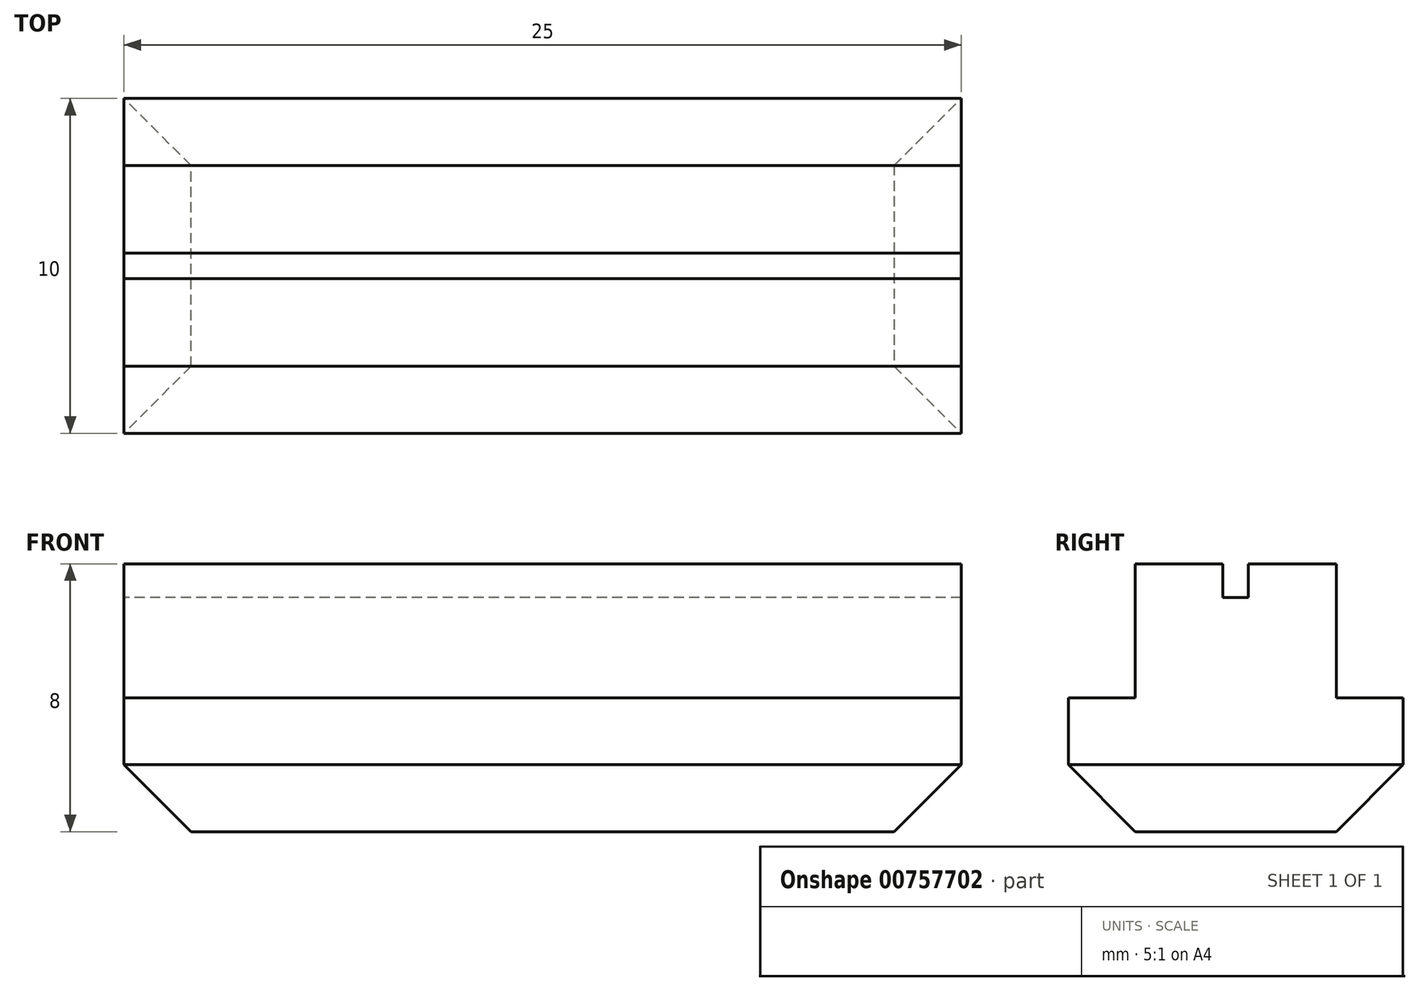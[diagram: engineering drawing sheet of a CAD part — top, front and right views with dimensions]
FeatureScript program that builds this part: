
annotation { "Feature Type Name" : "Feature", "Feature Type Description" : "" }
export const myFeature = defineFeature(function(context is Context, id is Id, definition is map)
    precondition{}
    {
        {
            var Q0;
            Q0=qCreatedBy(makeId("Front.planeOp"),FACE);
            var sketch = newSketch(context, id + "F0", { "sketchPlane" : qUnion([Q0])});
            skLineSegment(sketch, "E0.bottom", {"start": v(-12.5, 26) * mm, "end": v(12.5, 26) * mm});
            skLineSegment(sketch, "E0.top", {"start": v(-12.5, 34) * mm, "end": v(12.5, 34) * mm});
            skLineSegment(sketch, "E0.left", {"start": v(-12.5, 26) * mm, "end": v(-12.5, 34) * mm});
            skLineSegment(sketch, "E0.right", {"start": v(12.5, 26) * mm, "end": v(12.5, 34) * mm});
            skPoint(sketch, "E0.middle", {"position": v(0, 30) * mm});
            skSolve(sketch);
        }
        {
            var Q0;
            Q0=makeQuery(id+"F0.imprint","IMPRINT",FACE,{"disambiguationData":[TD([[makeQuery(id+"F0.imprint","IMPRINT",EDGE,{"derivedFrom":sQuery(id+"F0.wireOp",EDGE,"E0.bottom")}),1.0]])]});
            extrude(context, id + "F1", {"entities" : qUnion([Q0]), "endBound" : BoundingType.SYMMETRIC, "depth" : 10 * mm, "offsetDistance" : 25 * mm});
        }
        {
            var Q0;
            Q0=makeQuery(id+"F1.opExtrude","SWEPT_EDGE",EDGE,{"disambiguationData":[OSD([sQuery(id+"F0.wireOp",EDGE,"E0.bottom"),sQuery(id+"F0.wireOp",EDGE,"E0.right")])]});
            var Q1;
            Q1=makeQuery(id+"F1.opExtrude","SWEPT_EDGE",EDGE,{"disambiguationData":[OSD([sQuery(id+"F0.wireOp",EDGE,"E0.bottom"),sQuery(id+"F0.wireOp",EDGE,"E0.left")])]});
            chamfer(context, id + "F2", {"entities" : qUnion([Q0, Q1]), "width" : 2 * mm, "tangentPropagation" : true});
        }
        {
            var Q0;
            Q0=makeQuery(id+"F1.opExtrude","CAP_EDGE",EDGE,{"disambiguationData":[OSD([sQuery(id+"F0.wireOp",EDGE,"E0.bottom")])],"isStart":false});
            var Q1;
            Q1=makeQuery(id+"F1.opExtrude","CAP_EDGE",EDGE,{"disambiguationData":[OSD([sQuery(id+"F0.wireOp",EDGE,"E0.bottom")])],"isStart":true});
            chamfer(context, id + "F3", {"entities" : qUnion([Q0, Q1]), "width" : 2 * mm, "tangentPropagation" : true});
        }
        {
            var Q0;
            Q0=makeQuery(id+"F1.opExtrude","SWEPT_FACE",FACE,{"disambiguationData":[OSD([sQuery(id+"F0.wireOp",EDGE,"E0.left")])]});
            var sketch = newSketch(context, id + "F4", { "sketchPlane" : qUnion([Q0])});
            skLineSegment(sketch, "E1.0", {"start": v(5, 34) * mm, "end": v(3, 34) * mm});
            skLineSegment(sketch, "E2.0", {"start": v(-5, 30) * mm, "end": v(-5, 34) * mm});
            skLineSegment(sketch, "E3.0", {"start": v(5, 30) * mm, "end": v(5, 34) * mm});
            skLineSegment(sketch, "E4", {"start": v(-5, 30) * mm, "end": v(-3, 30) * mm});
            skLineSegment(sketch, "E5", {"start": v(-3, 34) * mm, "end": v(-3, 30) * mm});
            skLineSegment(sketch, "E6", {"start": v(3, 34) * mm, "end": v(3, 30) * mm});
            skLineSegment(sketch, "E7", {"start": v(0, 34) * mm, "end": v(0, 33) * mm, "construction": true});
            skLineSegment(sketch, "E8", {"start": v(0, 33) * mm, "end": v(0.38, 33) * mm});
            skLineSegment(sketch, "E9", {"start": v(0.38, 33) * mm, "end": v(0.38, 34) * mm});
            skLineSegment(sketch, "E10", {"start": v(0, 33) * mm, "end": v(-0.38, 33) * mm});
            skLineSegment(sketch, "E11", {"start": v(-0.38, 33) * mm, "end": v(-0.38, 34) * mm});
            skLineSegment(sketch, "E12.trimOffspring", {"start": v(0.38, 34) * mm, "end": v(-0.38, 34) * mm});
            skLineSegment(sketch, "E13.trimOffspring", {"start": v(-3, 34) * mm, "end": v(-5, 34) * mm});
            skLineSegment(sketch, "E14.trimOffspring", {"start": v(3, 30) * mm, "end": v(5, 30) * mm});
            skSolve(sketch);
        }
        {
            var Q0;
            Q0 = qSketchRegion(id + "F4", true);
            extrude(context, id + "F5", {"entities" : qUnion([Q0]), "operationType" : NewBodyOperationType.REMOVE, "oppositeDirection" : true, "depth" : 25 * mm, "offsetDistance" : 25 * mm});
        }
    });
